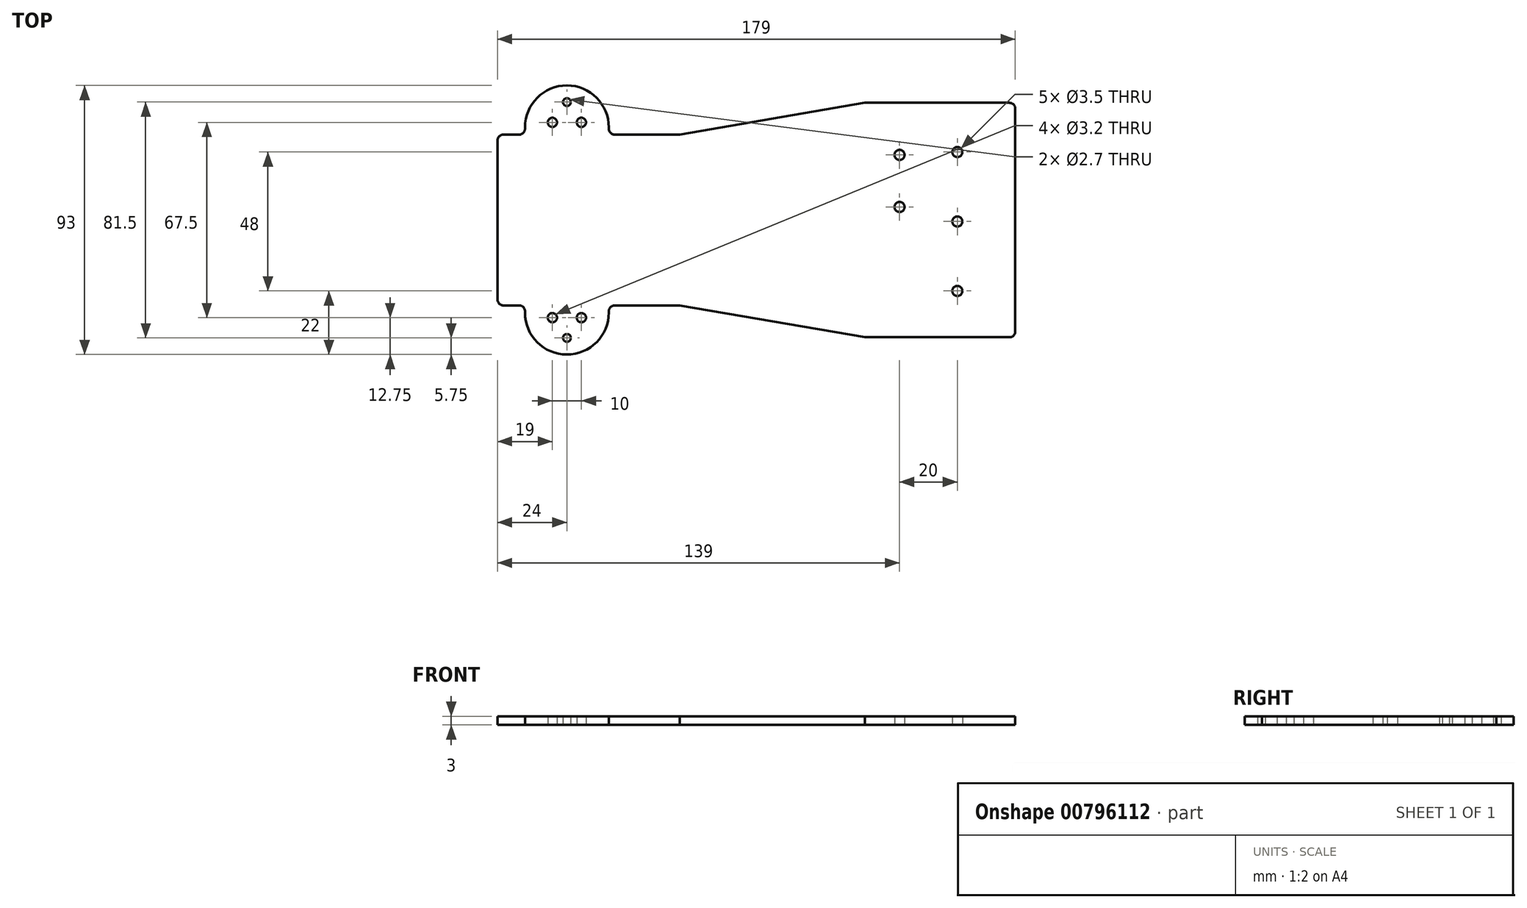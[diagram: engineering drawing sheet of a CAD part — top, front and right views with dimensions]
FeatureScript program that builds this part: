
annotation { "Feature Type Name" : "Feature", "Feature Type Description" : "" }
export const myFeature = defineFeature(function(context is Context, id is Id, definition is map)
    precondition{}
    {
        {
            var Q0;
            Q0=qCreatedBy(makeId("Top.planeOp"),FACE);
            var sketch = newSketch(context, id + "F0", { "sketchPlane" : qUnion([Q0])});
            skLineSegment(sketch, "E0", {"start": v(0, 0) * mm, "end": v(275.4, 0) * mm});
            skLineSegment(sketch, "E1", {"start": v(0, 0) * mm, "end": v(0, 27.5) * mm});
            skLineSegment(sketch, "E2", {"start": v(2, 29.5) * mm, "end": v(7.5, 29.5) * mm});
            skLineSegment(sketch, "E3", {"start": v(9.5, 31.5) * mm, "end": v(9.5, 32) * mm});
            skLineSegment(sketch, "E4", {"start": v(9.5, 32) * mm, "end": v(38.5, 32) * mm});
            skLineSegment(sketch, "E5", {"start": v(38.5, 32) * mm, "end": v(38.5, 31.5) * mm});
            skLineSegment(sketch, "E6", {"start": v(40.5, 29.5) * mm, "end": v(63, 29.5) * mm});
            skLineSegment(sketch, "E7", {"start": v(63, 29.5) * mm, "end": v(63, 0) * mm});
            skArc(sketch, "E8", {"start": v(38.5, 32) * mm, "mid": v(24, 46.5) * mm, "end": v(9.5, 32) * mm});
            skLineSegment(sketch, "E9", {"start": v(127, 0) * mm, "end": v(127, 40.5) * mm});
            skLineSegment(sketch, "E10", {"start": v(127, 40.5) * mm, "end": v(177, 40.5) * mm});
            skLineSegment(sketch, "E11", {"start": v(179, 38.5) * mm, "end": v(179, 0) * mm});
            skLineSegment(sketch, "E12", {"start": v(63, 29.5) * mm, "end": v(127, 40.5) * mm});
            skLineSegment(sketch, "E13.MirrorCS", {"start": v(0, 0) * mm, "end": v(0, -27.5) * mm});
            skLineSegment(sketch, "E14.MirrorCS", {"start": v(2, -29.5) * mm, "end": v(7.5, -29.5) * mm});
            skLineSegment(sketch, "E15.MirrorCS", {"start": v(9.5, -31.5) * mm, "end": v(9.5, -32) * mm});
            skArc(sketch, "E16.MirrorCS", {"start": v(38.5, -32) * mm, "mid": v(24, -46.5) * mm, "end": v(9.5, -32) * mm});
            skLineSegment(sketch, "E17.MirrorCS", {"start": v(38.5, -32) * mm, "end": v(38.5, -31.5) * mm});
            skLineSegment(sketch, "E18.MirrorCS", {"start": v(40.5, -29.5) * mm, "end": v(63, -29.5) * mm});
            skLineSegment(sketch, "E19.MirrorCS", {"start": v(63, -29.5) * mm, "end": v(127, -40.5) * mm});
            skLineSegment(sketch, "E20.MirrorCS", {"start": v(127, -40.5) * mm, "end": v(177, -40.5) * mm});
            skLineSegment(sketch, "E21.MirrorCS", {"start": v(179, -38.5) * mm, "end": v(179, 0) * mm});
            skPoint(sketch, "E22.visualSharp", {"position": v(9.5, 29.5) * mm});
            skArc(sketch, "E22.filletArc", {"start": v(7.5, 29.5) * mm, "mid": v(8.91, 30.09) * mm, "end": v(9.5, 31.5) * mm});
            skPoint(sketch, "E23.visualSharp", {"position": v(38.5, 29.5) * mm});
            skArc(sketch, "E23.filletArc", {"start": v(38.5, 31.5) * mm, "mid": v(39.09, 30.09) * mm, "end": v(40.5, 29.5) * mm});
            skPoint(sketch, "E24.visualSharp", {"position": v(9.5, -29.5) * mm});
            skArc(sketch, "E24.filletArc", {"start": v(9.5, -31.5) * mm, "mid": v(8.91, -30.09) * mm, "end": v(7.5, -29.5) * mm});
            skPoint(sketch, "E25.visualSharp", {"position": v(38.5, -29.5) * mm});
            skArc(sketch, "E25.filletArc", {"start": v(40.5, -29.5) * mm, "mid": v(39.09, -30.09) * mm, "end": v(38.5, -31.5) * mm});
            skPoint(sketch, "E26.visualSharp", {"position": v(0, 29.5) * mm});
            skArc(sketch, "E26.filletArc", {"start": v(2, 29.5) * mm, "mid": v(0.59, 28.91) * mm, "end": v(0, 27.5) * mm});
            skPoint(sketch, "E27.visualSharp", {"position": v(0, -29.5) * mm});
            skArc(sketch, "E27.filletArc", {"start": v(0, -27.5) * mm, "mid": v(0.59, -28.91) * mm, "end": v(2, -29.5) * mm});
            skPoint(sketch, "E28.visualSharp", {"position": v(179, -40.5) * mm});
            skArc(sketch, "E28.filletArc", {"start": v(177, -40.5) * mm, "mid": v(178.41, -39.91) * mm, "end": v(179, -38.5) * mm});
            skPoint(sketch, "E29.visualSharp", {"position": v(179, 40.5) * mm});
            skArc(sketch, "E29.filletArc", {"start": v(179, 38.5) * mm, "mid": v(178.41, 39.91) * mm, "end": v(177, 40.5) * mm});
            skLineSegment(sketch, "E30", {"start": v(24, -54.8) * mm, "end": v(24, 56.39) * mm});
            skCircle(sketch, "E31", {"center": v(19, -33.75) * mm, "radius": 1.6 * mm});
            skCircle(sketch, "E32", {"center": v(24, -40.75) * mm, "radius": 1.35 * mm});
            skCircle(sketch, "E33.MirrorC", {"center": v(29, -33.75) * mm, "radius": 1.6 * mm});
            skCircle(sketch, "E34.MirrorC", {"center": v(19, 33.75) * mm, "radius": 1.6 * mm});
            skCircle(sketch, "E35.MirrorC", {"center": v(29, 33.75) * mm, "radius": 1.6 * mm});
            skCircle(sketch, "E36.MirrorC", {"center": v(24, 40.75) * mm, "radius": 1.35 * mm});
            skLineSegment(sketch, "E37", {"start": v(159, -40.5) * mm, "end": v(159, 40.5) * mm});
            skLineSegment(sketch, "E38", {"start": v(139, -40.5) * mm, "end": v(139, 40.5) * mm});
            skCircle(sketch, "E39", {"center": v(159, -24.5) * mm, "radius": 1.75 * mm});
            skCircle(sketch, "E40", {"center": v(159, -0.5) * mm, "radius": 1.75 * mm});
            skCircle(sketch, "E41", {"center": v(159, 23.5) * mm, "radius": 1.75 * mm});
            skCircle(sketch, "E42", {"center": v(139, 4.5) * mm, "radius": 1.75 * mm});
            skCircle(sketch, "E43", {"center": v(139, 22.5) * mm, "radius": 1.75 * mm});
            skLineSegment(sketch, "E44", {"start": v(139, 4.5) * mm, "end": v(140.75, 4.5) * mm});
            skSolve(sketch);
        }
        {
            var Q0;
            Q0 = qSketchRegion(id + "F0", true);
            extrude(context, id + "F1", {"entities" : qUnion([Q0]), "depth" : 3 * mm, "offsetDistance" : 25 * mm});
        }
    });
